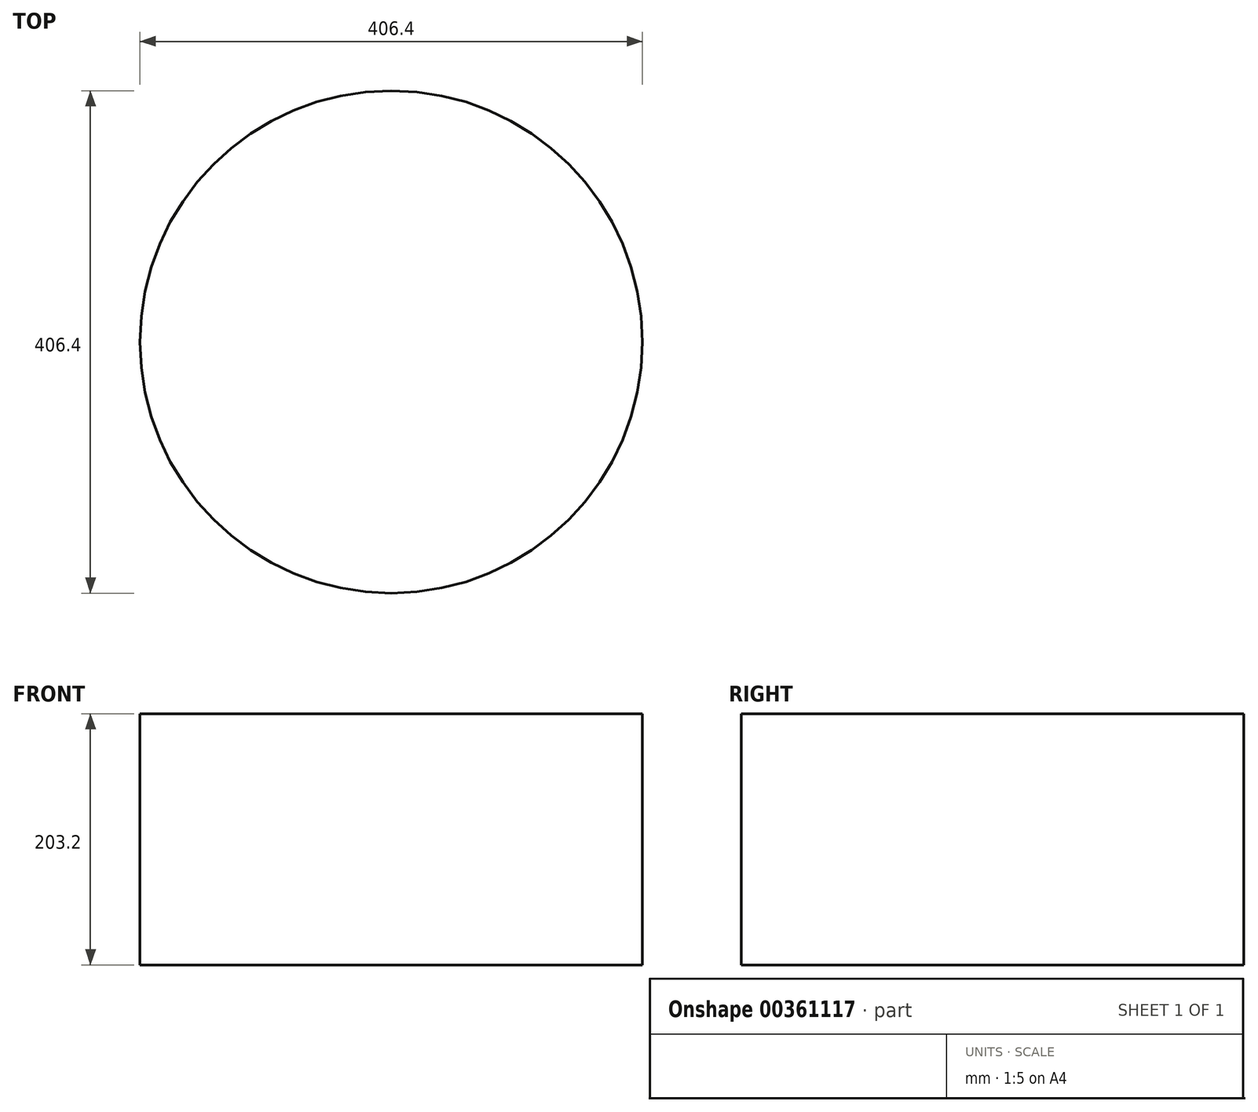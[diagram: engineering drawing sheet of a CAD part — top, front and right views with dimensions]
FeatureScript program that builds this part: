
annotation { "Feature Type Name" : "Feature", "Feature Type Description" : "" }
export const myFeature = defineFeature(function(context is Context, id is Id, definition is map)
    precondition{}
    {
        {
            var Q0;
            Q0=qCreatedBy(makeId("Top.planeOp"),FACE);
            var sketch = newSketch(context, id + "F0", { "sketchPlane" : qUnion([Q0])});
            skCircle(sketch, "E0", {"center": v(0, 0) * mm, "radius": 203.2 * mm});
            skSolve(sketch);
        }
        {
            var Q0;
            Q0 = qSketchRegion(id + "F0", true);
            extrude(context, id + "F1", {"entities" : qUnion([Q0]), "depth" : 203.2 * mm});
        }
    });
